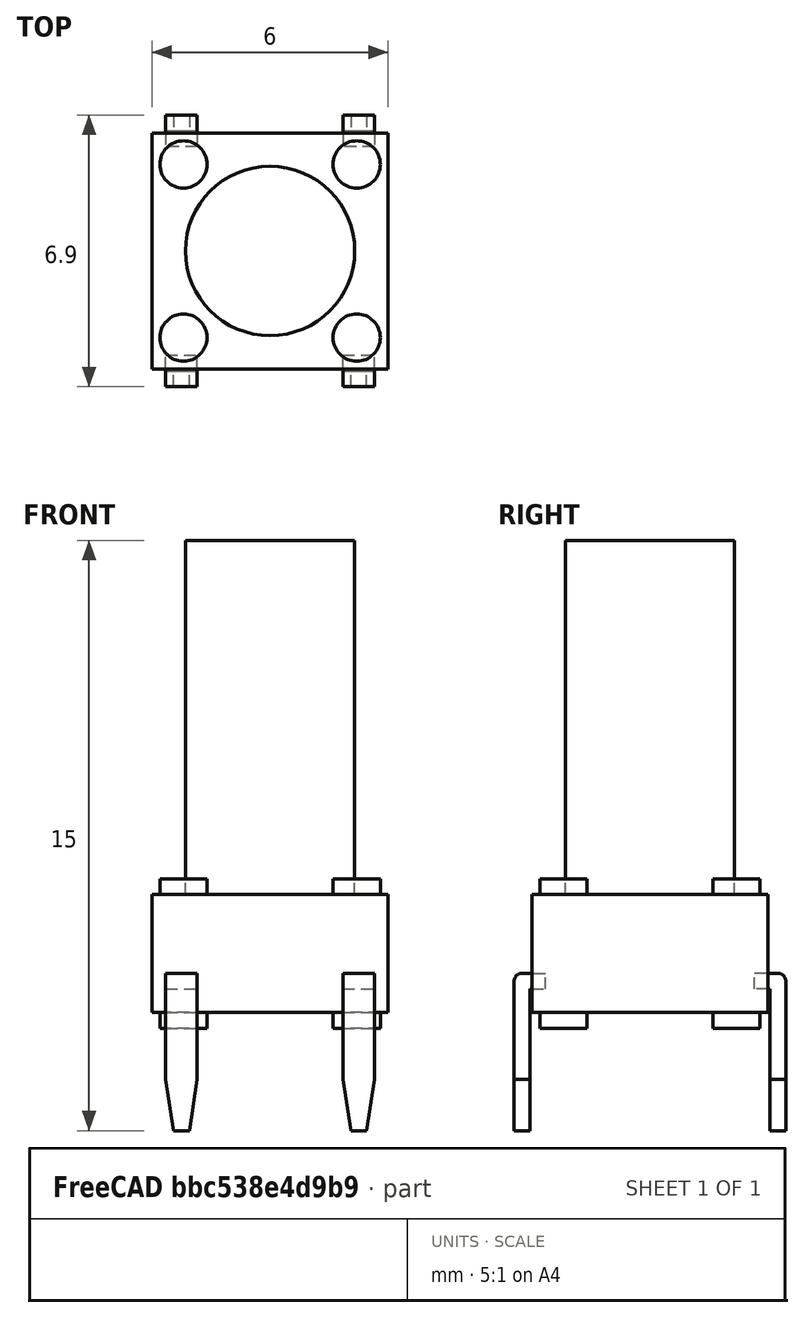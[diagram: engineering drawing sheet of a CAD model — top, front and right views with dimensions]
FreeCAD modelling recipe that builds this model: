
FCSTD DOCUMENT  (FreeCAD 0.16R6706 (Git))
Label: micro_switch_4.5_6.5
License: All rights reserved
LicenseURL: http://en.wikipedia.org/wiki/All_rights_reserved
objects: Part::Cylinder×9, Part::Box×5, Part::Compound×3, Part::Chamfer×2, Part::Fillet×2, Part::Fuse×2, Part::FeaturePython×2
note: 25 computed .brp shape members not serialized (recipe doc carries the construction recipe); baked Part::Feature solids carry a one-line shape summary decoded from their .brp

FEATURE [Part::Box] Box  label="Cube"
  Height = 3
  Length = 6
  Placement = pos=(-3,-3,0) rot=(0,0,1;0rad)
  Width = 6
FEATURE [Part::Cylinder] Cylinder
  Angle = 360
  Height = 9
  Placement = pos=(0,0,3) rot=(0,0,1;0rad)
  Radius = 2.15
FEATURE [Part::Box] Box001  label="Cube001"
  Height = 4
  Length = 0.8
  Placement = pos=(-2.65,-3.45,-3) rot=(0,0,1;0rad)
  Width = 0.4
FEATURE [Part::Cylinder] Cylinder001
  Angle = 360
  Height = 0.4
  Placement = pos=(2.2,-2.2,3) rot=(0,0,1;0rad)
  Radius = 0.6
FEATURE [Part::Cylinder] Cylinder002
  Angle = 360
  Height = 0.4
  Placement = pos=(2.2,2.2,3) rot=(0,0,1;0rad)
  Radius = 0.6
FEATURE [Part::Cylinder] Cylinder003
  Angle = 360
  Height = 0.4
  Placement = pos=(-2.2,-2.2,3) rot=(0,0,1;0rad)
  Radius = 0.6
FEATURE [Part::Cylinder] Cylinder004
  Angle = 360
  Height = 0.4
  Placement = pos=(-2.2,2.2,3) rot=(0,0,1;0rad)
  Radius = 0.6
FEATURE [Part::Chamfer] Chamfer
  Base = -> Box001
  Edges = 2 edges: [Edge4 r1=1.3 r2=0.2,Edge8 r1=1.3 r2=0.2]
FEATURE [Part::Fillet] Fillet
  Base = -> Chamfer
  Edges = 1 edges r=0.2: [Edge9]
FEATURE [Part::Box] Box002  label="Cube002"
  Height = 0.4
  Length = 0.8
  Placement = pos=(-2.65,-3.05,0.6) rot=(0,0,1;0rad)
  Width = 0.4
FEATURE [Part::Fuse] Fusion
  Base = -> Fillet
  Tool = -> Box002
FEATURE [Part::FeaturePython] Array  # Draft array (typed FeaturePython)
  Angle = 360
  ArrayType = 0
  Axis = (0,0,1)
  Base = -> Fusion
  Center = (0,0,0)
  Fuse = false
  IntervalAxis = (0,0,0)
  IntervalX = (4.5,0,0)
  IntervalY = (0,1,0)
  IntervalZ = (0,0,0)
  NumberPolar = 1
  NumberX = 2
  NumberY = 1
  NumberZ = 1
FEATURE [Part::Box] Box003  label="Cube003"
  Height = 4
  Length = 0.8
  Placement = pos=(-2.65,-3.45,-3) rot=(0,0,1;0rad)
  Width = 0.4
FEATURE [Part::Chamfer] Chamfer001
  Base = -> Box003
  Edges = 2 edges: [Edge4 r1=1.3 r2=0.2,Edge8 r1=1.3 r2=0.2]
FEATURE [Part::Fillet] Fillet001
  Base = -> Chamfer001
  Edges = 1 edges r=0.2: [Edge9]
FEATURE [Part::Box] Box004  label="Cube004"
  Height = 0.4
  Length = 0.8
  Placement = pos=(-2.65,-3.05,0.6) rot=(0,0,1;0rad)
  Width = 0.4
FEATURE [Part::Fuse] Fusion001
  Base = -> Fillet001
  Placement = pos=(-4.5,0,0) rot=(0,0,1;3.14159rad)
  Tool = -> Box004
FEATURE [Part::FeaturePython] Array001  # Draft array (typed FeaturePython)
  Angle = 360
  ArrayType = 0
  Axis = (0,0,1)
  Base = -> Fusion001
  Center = (0,0,0)
  Fuse = false
  IntervalAxis = (0,0,0)
  IntervalX = (4.5,0,0)
  IntervalY = (0,0,0)
  IntervalZ = (0,0,0)
  NumberPolar = 1
  NumberX = 2
  NumberY = 1
  NumberZ = 1
FEATURE [Part::Compound] Compound
  Links = -> [Cylinder001,Cylinder002,Cylinder003,Cylinder004]
FEATURE [Part::Cylinder] Cylinder005
  Angle = 360
  Height = 0.4
  Placement = pos=(2.2,-2.2,3) rot=(0,0,1;0rad)
  Radius = 0.6
FEATURE [Part::Cylinder] Cylinder006
  Angle = 360
  Height = 0.4
  Placement = pos=(2.2,2.2,3) rot=(0,0,1;0rad)
  Radius = 0.6
FEATURE [Part::Cylinder] Cylinder007
  Angle = 360
  Height = 0.4
  Placement = pos=(-2.2,-2.2,3) rot=(0,0,1;0rad)
  Radius = 0.6
FEATURE [Part::Cylinder] Cylinder008
  Angle = 360
  Height = 0.4
  Placement = pos=(-2.2,2.2,3) rot=(0,0,1;0rad)
  Radius = 0.6
FEATURE [Part::Compound] Compound001
  Links = -> [Cylinder005,Cylinder006,Cylinder007,Cylinder008]
  Placement = pos=(0,0,-3.4) rot=(0,0,1;0rad)
FEATURE [Part::Compound] Compound002
  Links = -> [Box,Array,Array001,Compound,Compound001]
